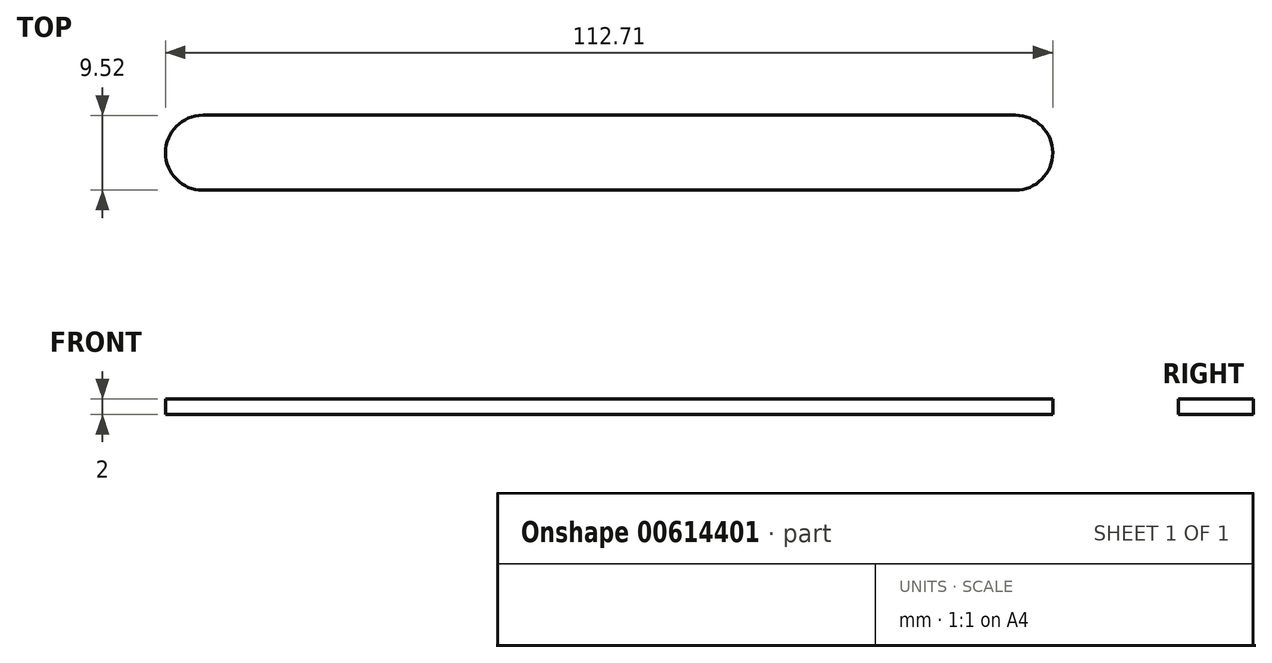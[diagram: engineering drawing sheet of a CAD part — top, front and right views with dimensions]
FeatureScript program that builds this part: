
annotation { "Feature Type Name" : "Feature", "Feature Type Description" : "" }
export const myFeature = defineFeature(function(context is Context, id is Id, definition is map)
    precondition{}
    {
        {
            var Q0;
            Q0=qCreatedBy(makeId("Top.planeOp"),FACE);
            var sketch = newSketch(context, id + "F0", { "sketchPlane" : qUnion([Q0])});
            skLineSegment(sketch, "E0", {"start": v(508.42, -171.5) * mm, "end": v(611.61, -171.5) * mm, "construction": true});
            skArc(sketch, "E1.0.startCap", {"start": v(508.42, -176.27) * mm, "mid": v(503.66, -171.5) * mm, "end": v(508.42, -166.75) * mm});
            skArc(sketch, "E1.0.endCap", {"start": v(611.61, -166.75) * mm, "mid": v(616.37, -171.5) * mm, "end": v(611.61, -176.27) * mm});
            skLineSegment(sketch, "E1.0.left", {"start": v(508.42, -166.75) * mm, "end": v(611.61, -166.75) * mm});
            skLineSegment(sketch, "E1.0.right", {"start": v(508.42, -176.27) * mm, "end": v(611.61, -176.27) * mm});
            skSolve(sketch);
        }
        {
            var Q0;
            Q0 = qSketchRegion(id + "F0", true);
            extrude(context, id + "F1", {"entities" : qUnion([Q0]), "depth" : 2 * mm, "offsetDistance" : 25.4 * mm});
        }
    });
